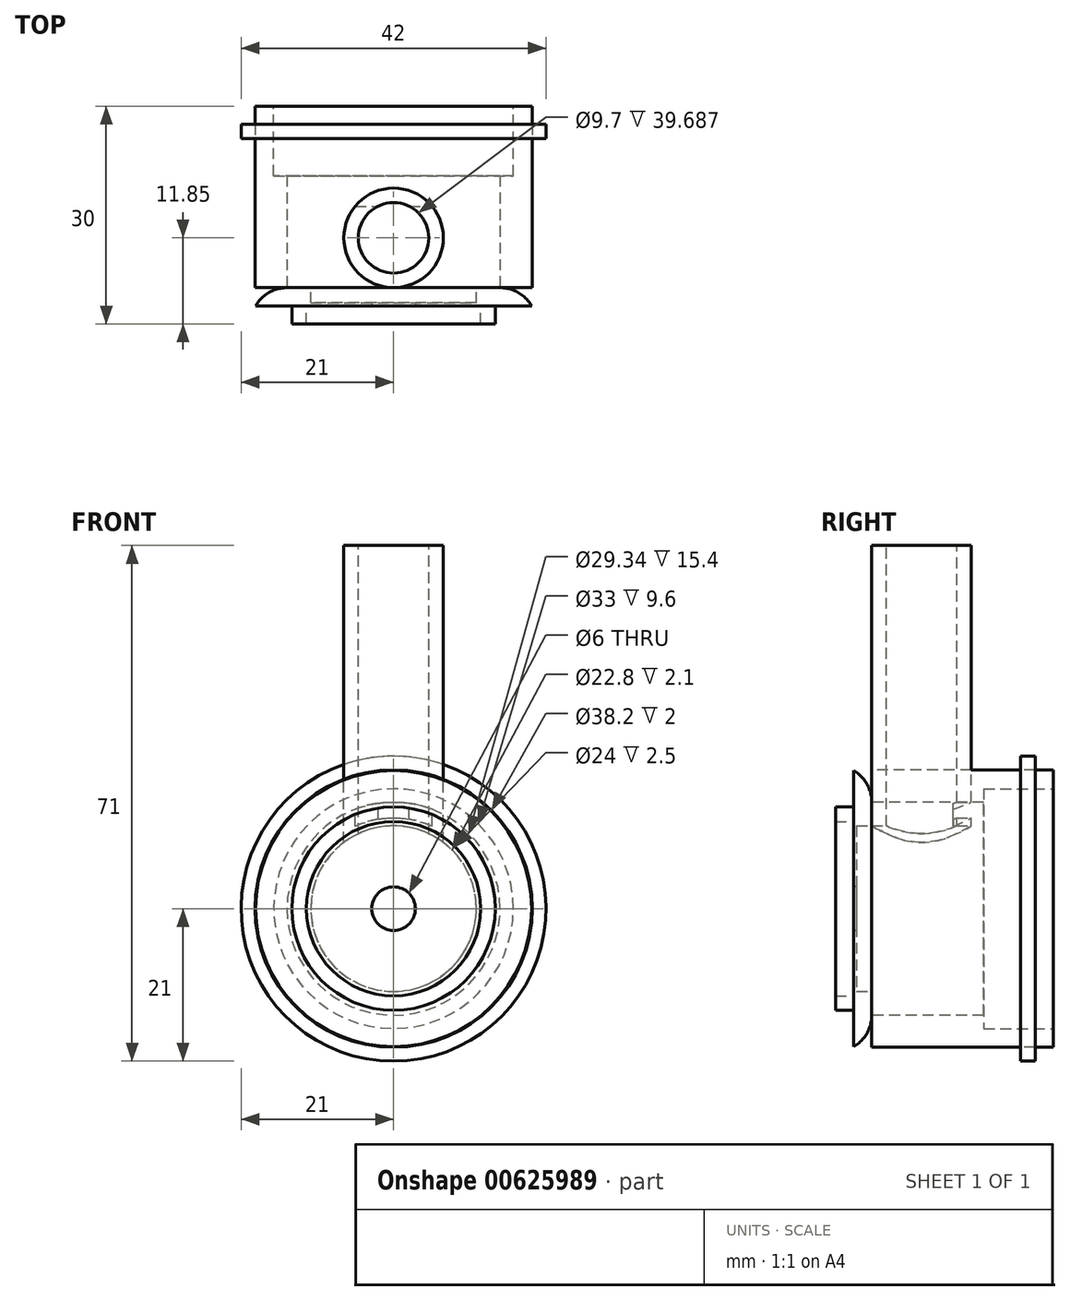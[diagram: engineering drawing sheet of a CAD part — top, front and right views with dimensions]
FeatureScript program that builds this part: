
annotation { "Feature Type Name" : "Feature", "Feature Type Description" : "" }
export const myFeature = defineFeature(function(context is Context, id is Id, definition is map)
    precondition{}
    {
        {
            var Q0;
            Q0=qCreatedBy(makeId("Front.planeOp"),FACE);
            var sketch = newSketch(context, id + "F0", { "sketchPlane" : qUnion([Q0])});
            skCircle(sketch, "E0", {"center": v(0, 0) * mm, "radius": 12 * mm});
            skCircle(sketch, "E1", {"center": v(0, 0) * mm, "radius": 14 * mm});
            skCircle(sketch, "E2", {"center": v(0, 0) * mm, "radius": 19 * mm});
            skCircle(sketch, "E3", {"center": v(0, 0) * mm, "radius": 3 * mm});
            skSolve(sketch);
        }
        {
            var Q0;
            Q0=makeQuery(id+"F0.imprint","IMPRINT",FACE,{"disambiguationData":[TD([[makeQuery(id+"F0.imprint","IMPRINT",EDGE,{"derivedFrom":sQuery(id+"F0.wireOp",EDGE,"E0")}),-1.0]])]});
            extrude(context, id + "F1", {"entities" : qUnion([Q0]), "depth" : 2.5 * mm, "offsetDistance" : 25 * mm});
        }
        {
            var Q0;
            Q0=makeQuery(id+"F0.imprint","IMPRINT",FACE,{"disambiguationData":[TD([[makeQuery(id+"F0.imprint","IMPRINT",EDGE,{"derivedFrom":sQuery(id+"F0.wireOp",EDGE,"E1")}),-1.0]])]});
            var Q1;
            Q1=makeQuery(id+"F0.imprint","IMPRINT",FACE,{"disambiguationData":[TD([[makeQuery(id+"F0.imprint","IMPRINT",EDGE,{"derivedFrom":sQuery(id+"F0.wireOp",EDGE,"E0")}),1.0]])]});
            var Q2;
            Q2=makeQuery(id+"F0.imprint","IMPRINT",FACE,{"disambiguationData":[TD([[makeQuery(id+"F0.imprint","IMPRINT",EDGE,{"derivedFrom":sQuery(id+"F0.wireOp",EDGE,"E3")}),1.0]])]});
            var Q3;
            Q3=makeQuery(id+"F0.imprint","IMPRINT",FACE,{"disambiguationData":[TD([[makeQuery(id+"F0.imprint","IMPRINT",EDGE,{"derivedFrom":sQuery(id+"F0.wireOp",EDGE,"E0")}),-1.0]])]});
            extrude(context, id + "F2", {"entities" : qUnion([Q0, Q1, Q2, Q3]), "oppositeDirection" : true, "depth" : 2.5 * mm, "offsetDistance" : 25 * mm});
        }
        {
            var Q0;
            Q0=makeQuery(id+"F0.imprint","IMPRINT",FACE,{"disambiguationData":[TD([[makeQuery(id+"F0.imprint","IMPRINT",EDGE,{"derivedFrom":sQuery(id+"F0.wireOp",EDGE,"E3")}),1.0]])]});
            var Q1;
            Q1 = qSketchRegion(id + "F4", true);
            extrude(context, id + "F3", {"entities" : qUnion([Q0, Q1]), "operationType" : NewBodyOperationType.REMOVE, "oppositeDirection" : true, "depth" : 2.5 * mm, "offsetDistance" : 25 * mm});
        }
        {
            var Q0;
            Q0=qCreatedBy(makeId("Front.planeOp"),FACE);
            var sketch = newSketch(context, id + "F4", { "sketchPlane" : qUnion([Q0])});
            skCircle(sketch, "E4", {"center": v(0, 0) * mm, "radius": 12.5 * mm});
            skCircle(sketch, "E5", {"center": v(0, 0) * mm, "radius": 11.4 * mm});
            skSolve(sketch);
        }
        {
            var Q0;
            Q0=qCreatedBy(makeId("Right.planeOp"),FACE);
            var sketch = newSketch(context, id + "F5", { "sketchPlane" : qUnion([Q0])});
            skLineSegment(sketch, "E6", {"start": v(9.35, 172.54) * mm, "end": v(9.35, -168.73) * mm, "construction": true});
            skPoint(sketch, "E7", {"position": v(9.35, 50) * mm});
            skSolve(sketch);
        }
        {
            var Q0;
            Q0=makeQuery(id+"F2.opExtrude","CAP_EDGE",EDGE,{"disambiguationData":[OSD([sQuery(id+"F0.wireOp",EDGE,"E2")])],"isStart":false});
            fillet(context, id + "F6", {"entities" : qUnion([Q0]), "radius" : 5 * mm, "tangentPropagation" : true, "allowEdgeOverflow" : false});
        }
        {
            var Q0;
            Q0=qCreatedBy(makeId("Top.planeOp"),FACE);
            cPlane(context, id + "F7", {"entities" : qUnion([Q0]), "cplaneType" : CPlaneType.OFFSET, "offset" : 50 * mm, "width" : 150 * mm, "height" : 150 * mm});
        }
        {
            var Q0;
            Q0=qCreatedBy(id+"F7.planeOp",FACE);
            var sketch = newSketch(context, id + "F8", { "sketchPlane" : qUnion([Q0])});
            skCircle(sketch, "E8", {"center": v(0, 9.35) * mm, "radius": 4.85 * mm});
            skCircle(sketch, "E9", {"center": v(0, 9.35) * mm, "radius": 6.85 * mm});
            skSolve(sketch);
        }
        {
            var Q0;
            Q0=makeQuery(id+"F8.imprint","IMPRINT",FACE,{"disambiguationData":[TD([[makeQuery(id+"F8.imprint","IMPRINT",EDGE,{"derivedFrom":sQuery(id+"F8.wireOp",EDGE,"E8")}),-1.0]])]});
            extrude(context, id + "F9", {"entities" : qUnion([Q0]), "oppositeDirection" : true, "depth" : 53.6 * mm, "offsetDistance" : 25 * mm});
        }
        {
            var Q0;
            Q0=makeQuery(id+"F2.opExtrude","CAP_FACE",FACE,{"disambiguationData":[OSD([sQuery(id+"F0.wireOp",EDGE,"E2")])],"isStart":false});
            var sketch = newSketch(context, id + "F10", { "sketchPlane" : qUnion([Q0])});
            skCircle(sketch, "E10", {"center": v(0, 0) * mm, "radius": 19.1 * mm});
            skSolve(sketch);
        }
        {
            var Q0;
            Q0=makeQuery(id+"F10.imprint","IMPRINT",FACE,{"disambiguationData":[TD([[makeQuery(id+"F10.imprint","IMPRINT",EDGE,{"derivedFrom":sQuery(id+"F10.wireOp",EDGE,"E10")}),1.0]])]});
            var Q1;
            Q1=makeQuery(id+"F10.imprint","IMPRINT",FACE,{"disambiguationData":[TD([[makeQuery(id+"F10.imprint","IMPRINT",EDGE,{"derivedFrom":makeQuery(id+"F3.boolean.opBoolean","COPY",EDGE,{"derivedFrom":makeQuery(id+"F3.opExtrude","CAP_EDGE",EDGE,{"disambiguationData":[OSD([sQuery(id+"F0.wireOp",EDGE,"E3")])],"isStart":false})})}),1.0]])]});
            var Q2;
            Q2=makeQuery(id+"F10.imprint","IMPRINT",FACE,{"disambiguationData":[TD([[makeQuery(id+"F10.imprint","IMPRINT",EDGE,{"derivedFrom":makeQuery(id+"F3.boolean.opBoolean","COPY",EDGE,{"derivedFrom":makeQuery(id+"F3.opExtrude","CAP_EDGE",EDGE,{"disambiguationData":[OSD([sQuery(id+"F0.wireOp",EDGE,"E3")])],"isStart":false})})}),-1.0]])]});
            extrude(context, id + "F11", {"entities" : qUnion([Q0, Q1, Q2]), "depth" : 25 * mm, "offsetDistance" : 25 * mm});
        }
        {
            var Q0;
            Q0=makeQuery(id+"F11.opExtrude","CAP_FACE",FACE,{"disambiguationData":[OSD([sQuery(id+"F10.wireOp",EDGE,"E10")])],"isStart":false});
            var sketch = newSketch(context, id + "F12", { "sketchPlane" : qUnion([Q0])});
            skCircle(sketch, "E11", {"center": v(0, 0) * mm, "radius": 16.5 * mm});
            skSolve(sketch);
        }
        {
            var Q0;
            Q0=makeQuery(id+"F12.imprint","IMPRINT",FACE,{"disambiguationData":[TD([[makeQuery(id+"F12.imprint","IMPRINT",EDGE,{"derivedFrom":sQuery(id+"F12.wireOp",EDGE,"E11")}),1.0]])]});
            extrude(context, id + "F13", {"entities" : qUnion([Q0]), "operationType" : NewBodyOperationType.REMOVE, "oppositeDirection" : true, "depth" : 9.6 * mm, "offsetDistance" : 25 * mm});
        }
        {
            var Q0;
            Q0=makeQuery(id+"F13.boolean.opBoolean","COPY",FACE,{"derivedFrom":makeQuery(id+"F13.opExtrude","CAP_FACE",FACE,{"disambiguationData":[OSD([sQuery(id+"F12.wireOp",EDGE,"E11")])],"isStart":false})});
            var sketch = newSketch(context, id + "F14", { "sketchPlane" : qUnion([Q0])});
            skCircle(sketch, "E12", {"center": v(0, 0) * mm, "radius": 12.5 * mm});
            skCircle(sketch, "E13", {"center": v(0, 0) * mm, "radius": 11.4 * mm});
            skSolve(sketch);
        }
        {
            var Q0;
            Q0=makeQuery(id+"F14.imprint","IMPRINT",FACE,{"disambiguationData":[TD([[makeQuery(id+"F14.imprint","IMPRINT",EDGE,{"derivedFrom":sQuery(id+"F14.wireOp",EDGE,"E12")}),-1.0]])]});
            extrude(context, id + "F15", {"entities" : qUnion([Q0]), "operationType" : NewBodyOperationType.REMOVE, "oppositeDirection" : true, "depth" : 4.2 * mm, "offsetDistance" : 25 * mm});
        }
        {
            var Q0;
            Q0=makeQuery(id+"F14.imprint","IMPRINT",FACE,{"disambiguationData":[TD([[makeQuery(id+"F14.imprint","IMPRINT",EDGE,{"derivedFrom":sQuery(id+"F14.wireOp",EDGE,"E13")}),1.0]])]});
            extrude(context, id + "F16", {"entities" : qUnion([Q0]), "operationType" : NewBodyOperationType.REMOVE, "oppositeDirection" : true, "depth" : 17.5 * mm, "offsetDistance" : 25 * mm});
        }
        {
            var Q0;
            Q0=makeQuery(id+"F11.opExtrude","CAP_FACE",FACE,{"disambiguationData":[OSD([sQuery(id+"F10.wireOp",EDGE,"E10")])],"isStart":false});
            var sketch = newSketch(context, id + "F17", { "sketchPlane" : qUnion([Q0])});
            skCircle(sketch, "E14", {"center": v(0, 0) * mm, "radius": 21 * mm});
            skSolve(sketch);
        }
        {
            var Q0;
            Q0=makeQuery(id+"F17.imprint","IMPRINT",FACE,{"disambiguationData":[TD([[makeQuery(id+"F17.imprint","IMPRINT",EDGE,{"derivedFrom":sQuery(id+"F17.wireOp",EDGE,"E14")}),1.0]])]});
            extrude(context, id + "F18", {"entities" : qUnion([Q0]), "oppositeDirection" : true, "depth" : 4.5 * mm, "offsetDistance" : 25 * mm, "hasSecondDirection" : true, "secondDirectionOppositeDirection" : true, "secondDirectionDepth" : 2.5 * mm});
        }
    });
